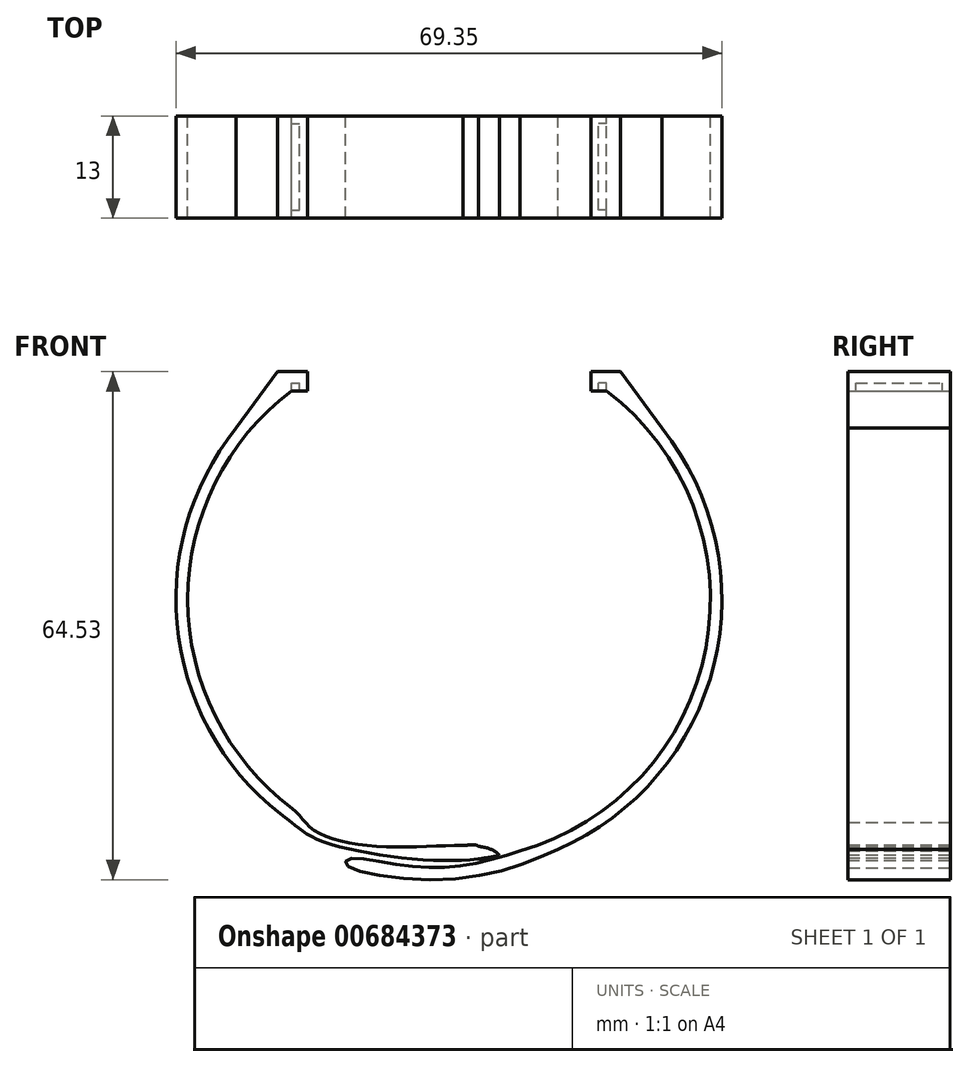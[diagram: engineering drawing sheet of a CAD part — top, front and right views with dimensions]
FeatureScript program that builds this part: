
annotation { "Feature Type Name" : "Feature", "Feature Type Description" : "" }
export const myFeature = defineFeature(function(context is Context, id is Id, definition is map)
    precondition{}
    {
        {
            var Q0;
            Q0=qCreatedBy(makeId("Front.planeOp"),FACE);
            var sketch = newSketch(context, id + "F0", { "sketchPlane" : qUnion([Q0])});
            skArc(sketch, "E0", {"start": v(-25.87, 22) * mm, "mid": v(-33.2, -4.57) * mm, "end": v(-18.84, -28.1) * mm});
            skArc(sketch, "E1.1", {"start": v(-18.84, 26.74) * mm, "mid": v(-32.03, 0.21) * mm, "end": v(-18.78, -26.29) * mm});
            skPoint(sketch, "E2.top.start.orphan", {"position": v(21.16, -28.1) * mm});
            skPoint(sketch, "E3.trimOffspring.end.orphan", {"position": v(-18.84, -28.1) * mm});
            skFitSpline(sketch, "E4", {"points": [v(10.14, -31.7) * mm, v(1.16, -32.94) * mm, v(-14.97, -30.47) * mm, v(-18.84, -28.1) * mm], "startDerivative": vector(-23.65, -5.7) * mm, "endDerivative": vector(-12.46, 10.4) * mm});
            skPoint(sketch, "E5.2.internal.orphan", {"position": v(-0.34, -31.75) * mm});
            skFitSpline(sketch, "E6", {"points": [v(-18.78, -26.29) * mm, v(-16.1, -28.99) * mm, v(-6.83, -31.2) * mm, v(4.9, -31.14) * mm, v(7.55, -32.33) * mm], "startDerivative": vector(17.01, -12.6) * mm, "endDerivative": vector(5.13, -10.96) * mm});
            skArc(sketch, "E7.trimOffspring", {"start": v(15.01, -31.52) * mm, "mid": v(34.81, -8.01) * mm, "end": v(28.18, 22) * mm});
            skPoint(sketch, "E8.1.internal.orphan", {"position": v(-14.97, -31.62) * mm});
            skPoint(sketch, "E8.2.internal.orphan", {"position": v(-0.34, -34.44) * mm});
            skArc(sketch, "E9.trimOffspring", {"start": v(10.14, -31.7) * mm, "mid": v(33.78, -5.9) * mm, "end": v(21.16, 26.74) * mm});
            skFitSpline(sketch, "E10", {"points": [v(4.82, -32.74) * mm, v(4.9, -31.14) * mm, v(2.9, -31.03) * mm], "startDerivative": vector(1.1, 3.62) * mm, "endDerivative": vector(-4.68, -0.25) * mm});
            skFitSpline(sketch, "E11", {"points": [v(10.14, -31.7) * mm, v(2.9, -33.56) * mm, v(-5.14, -33.48) * mm, v(-11.6, -32.74) * mm, v(-11.95, -33.42) * mm, v(0.78, -35.32) * mm, v(15.01, -31.52) * mm], "startDerivative": vector(-36, -13.01) * mm, "endDerivative": vector(49.5, 22.79) * mm});
            skLineSegment(sketch, "E12", {"start": v(-20.62, 29.17) * mm, "end": v(-25.87, 22) * mm});
            skLineSegment(sketch, "E13", {"start": v(-25.87, 22) * mm, "end": v(-23.92, 22) * mm, "construction": true});
            skLineSegment(sketch, "E14", {"start": v(22.94, 29.17) * mm, "end": v(28.18, 22) * mm});
            skLineSegment(sketch, "E15.trimOffspring", {"start": v(26.24, 22) * mm, "end": v(28.18, 22) * mm, "construction": true});
            skLineSegment(sketch, "E16.right", {"start": v(-16.84, 29.17) * mm, "end": v(-16.84, 26.74) * mm});
            skPoint(sketch, "E17.start.orphan", {"position": v(-18.84, 28.6) * mm});
            skLineSegment(sketch, "E18", {"start": v(-18.84, 27.74) * mm, "end": v(-18.84, 26.74) * mm});
            skPoint(sketch, "E19.start.orphan", {"position": v(21.16, 28.6) * mm});
            skLineSegment(sketch, "E20", {"start": v(21.16, 27.74) * mm, "end": v(21.16, 26.74) * mm});
            skPoint(sketch, "E21.start.orphan", {"position": v(20.16, 26.74) * mm});
            skLineSegment(sketch, "E22", {"start": v(21.16, 27.74) * mm, "end": v(20.16, 27.74) * mm});
            skLineSegment(sketch, "E23", {"start": v(20.16, 27.74) * mm, "end": v(20.16, 26.74) * mm});
            skLineSegment(sketch, "E24", {"start": v(20.16, 26.74) * mm, "end": v(19.16, 26.74) * mm});
            skPoint(sketch, "E16.top.start.orphan", {"position": v(-17.84, 26.74) * mm});
            skLineSegment(sketch, "E25", {"start": v(-18.84, 27.74) * mm, "end": v(-17.84, 27.74) * mm});
            skLineSegment(sketch, "E26", {"start": v(-17.84, 27.74) * mm, "end": v(-17.84, 26.74) * mm});
            skLineSegment(sketch, "E27", {"start": v(-17.84, 26.74) * mm, "end": v(-16.84, 26.74) * mm});
            skLineSegment(sketch, "E28", {"start": v(19.16, 29.17) * mm, "end": v(22.94, 29.17) * mm});
            skPoint(sketch, "E29.bottom.end.orphan", {"position": v(19.16, 31.6) * mm});
            skLineSegment(sketch, "E30", {"start": v(19.16, 29.17) * mm, "end": v(19.16, 26.74) * mm});
            skLineSegment(sketch, "E31", {"start": v(19.16, 29.17) * mm, "end": v(-16.84, 29.17) * mm, "construction": true});
            skLineSegment(sketch, "E32", {"start": v(-16.84, 29.17) * mm, "end": v(-20.62, 29.17) * mm});
            skPoint(sketch, "E33.orphan", {"position": v(-16.84, 31.6) * mm});
            skSolve(sketch);
        }
        {
            var Q0;
            Q0 = qSketchRegion(id + "F0", true);
            extrude(context, id + "F1", {"entities" : qUnion([Q0]), "depth" : 13 * mm, "offsetDistance" : 25 * mm});
        }
        {
            var Q0;
            Q0=makeQuery(id+"F1.opExtrude","SWEPT_FACE",FACE,{"disambiguationData":[OSD([sQuery(id+"F0.wireOp",EDGE,"E25")])]});
            var sketch = newSketch(context, id + "F2", { "sketchPlane" : qUnion([Q0])});
            skLineSegment(sketch, "E34.bottom", {"start": v(-18.84, 13) * mm, "end": v(-17.84, 13) * mm});
            skLineSegment(sketch, "E34.top", {"start": v(-18.84, 12) * mm, "end": v(-17.84, 12) * mm});
            skLineSegment(sketch, "E34.left", {"start": v(-18.84, 13) * mm, "end": v(-18.84, 12) * mm});
            skLineSegment(sketch, "E34.right", {"start": v(-17.84, 13) * mm, "end": v(-17.84, 12) * mm});
            skLineSegment(sketch, "E35.bottom", {"start": v(-18.84, 0) * mm, "end": v(-17.84, 0) * mm});
            skLineSegment(sketch, "E35.top", {"start": v(-18.84, 1) * mm, "end": v(-17.84, 1) * mm});
            skLineSegment(sketch, "E35.left", {"start": v(-18.84, 0) * mm, "end": v(-18.84, 1) * mm});
            skLineSegment(sketch, "E35.right", {"start": v(-17.84, 0) * mm, "end": v(-17.84, 1) * mm});
            skSolve(sketch);
        }
        {
            var Q0;
            Q0 = qSketchRegion(id + "F2", true);
            extrude(context, id + "F3", {"entities" : qUnion([Q0]), "operationType" : NewBodyOperationType.ADD, "depth" : 1 * mm, "offsetDistance" : 25 * mm});
        }
        {
            var Q0;
            Q0=makeQuery(id+"F1.opExtrude","SWEPT_FACE",FACE,{"disambiguationData":[OSD([sQuery(id+"F0.wireOp",EDGE,"E22")])]});
            var sketch = newSketch(context, id + "F4", { "sketchPlane" : qUnion([Q0])});
            skLineSegment(sketch, "E36.bottom", {"start": v(21.16, 0) * mm, "end": v(20.16, 0) * mm});
            skLineSegment(sketch, "E36.top", {"start": v(21.16, 1) * mm, "end": v(20.16, 1) * mm});
            skLineSegment(sketch, "E36.left", {"start": v(21.16, 0) * mm, "end": v(21.16, 1) * mm});
            skLineSegment(sketch, "E36.right", {"start": v(20.16, 0) * mm, "end": v(20.16, 1) * mm});
            skLineSegment(sketch, "E37.bottom", {"start": v(21.16, 13) * mm, "end": v(20.16, 13) * mm});
            skLineSegment(sketch, "E37.top", {"start": v(21.16, 12) * mm, "end": v(20.16, 12) * mm});
            skLineSegment(sketch, "E37.left", {"start": v(21.16, 13) * mm, "end": v(21.16, 12) * mm});
            skLineSegment(sketch, "E37.right", {"start": v(20.16, 13) * mm, "end": v(20.16, 12) * mm});
            skSolve(sketch);
        }
        {
            var Q0;
            Q0 = qSketchRegion(id + "F4", true);
            extrude(context, id + "F5", {"entities" : qUnion([Q0]), "operationType" : NewBodyOperationType.ADD, "depth" : 1 * mm, "offsetDistance" : 25 * mm});
        }
    });
